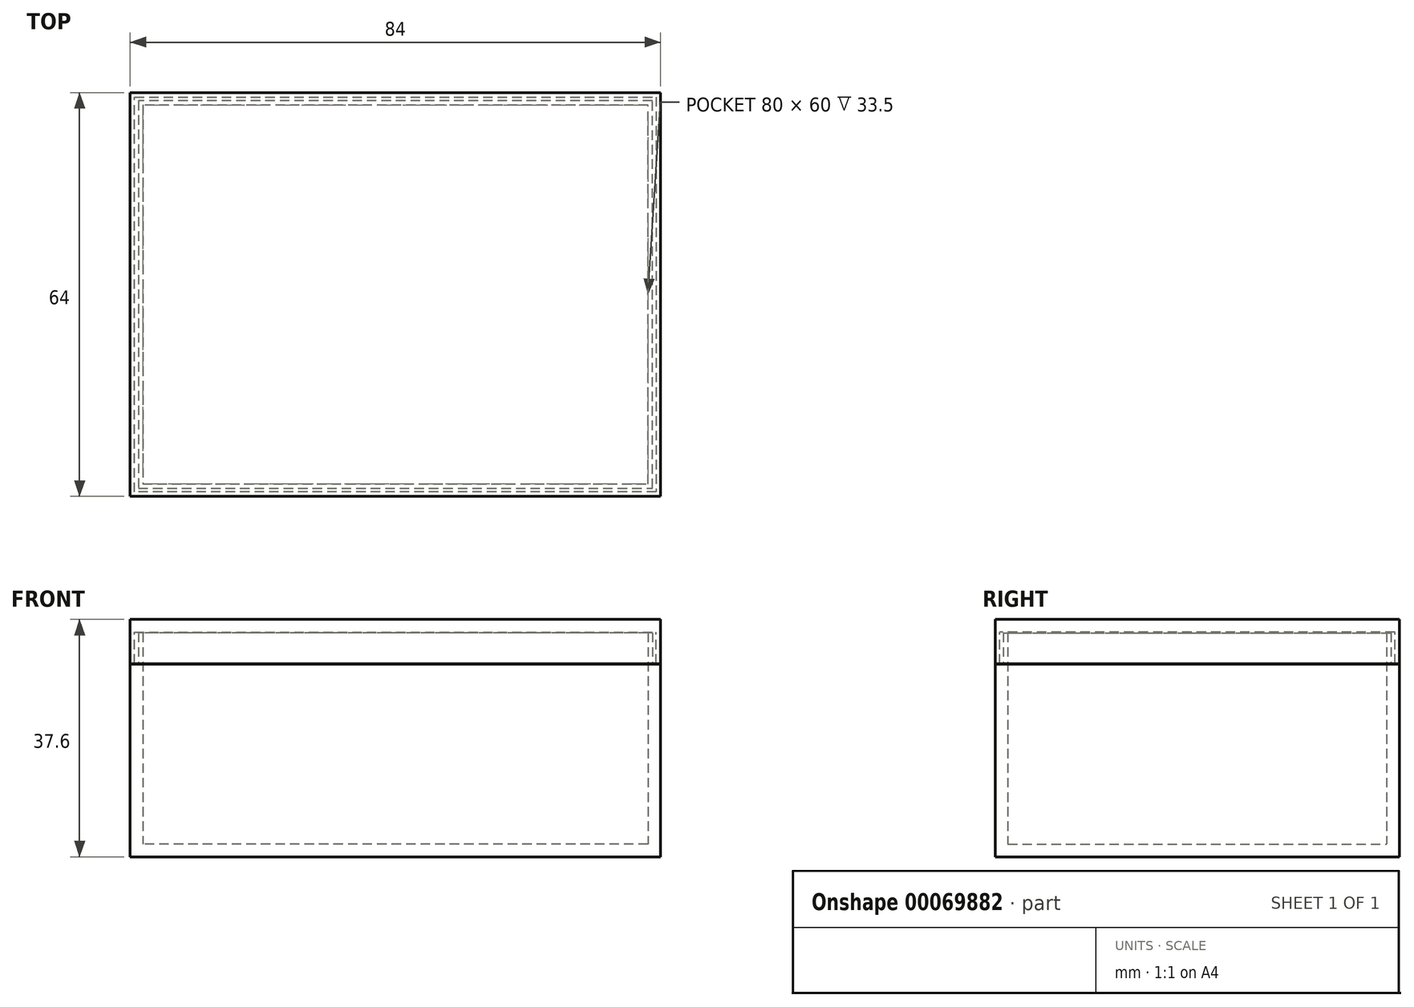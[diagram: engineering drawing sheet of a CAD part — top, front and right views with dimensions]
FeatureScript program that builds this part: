
annotation { "Feature Type Name" : "Feature", "Feature Type Description" : "" }
export const myFeature = defineFeature(function(context is Context, id is Id, definition is map)
    precondition{}
    {
        {
            var Q0;
            Q0=qCreatedBy(makeId("Top.planeOp"),FACE);
            var sketch = newSketch(context, id + "F0", { "sketchPlane" : qUnion([Q0])});
            skLineSegment(sketch, "E0.rect.bottom", {"start": v(42, -32) * mm, "end": v(-42, -32) * mm});
            skLineSegment(sketch, "E0.rect.top", {"start": v(42, 32) * mm, "end": v(-42, 32) * mm});
            skLineSegment(sketch, "E0.rect.left", {"start": v(42, -32) * mm, "end": v(42, 32) * mm});
            skLineSegment(sketch, "E0.rect.right", {"start": v(-42, -32) * mm, "end": v(-42, 32) * mm});
            skPoint(sketch, "E0.rect.middle", {"position": v(0, 0) * mm});
            skSolve(sketch);
        }
        {
            var Q0;
            Q0=qSketchRegion(id+"F0",true);
            extrude(context, id + "F1", {"entities" : qUnion([Q0]), "depth" : 2 * mm});
        }
        {
            var Q0;
            Q0=makeQuery(id+"F1.opExtrude","CAP_FACE",FACE,{"disambiguationData":[OSD([sQuery(id+"F0.wireOp",EDGE,"E0.rect.bottom"),sQuery(id+"F0.wireOp",EDGE,"E0.rect.top"),sQuery(id+"F0.wireOp",EDGE,"E0.rect.left"),sQuery(id+"F0.wireOp",EDGE,"E0.rect.right")])],"isStart":false});
            var sketch = newSketch(context, id + "F2", { "sketchPlane" : qUnion([Q0])});
            skLineSegment(sketch, "E1.0.0", {"start": v(-42, -32) * mm, "end": v(42, -32) * mm});
            skLineSegment(sketch, "E1.0.1", {"start": v(42, -32) * mm, "end": v(42, 32) * mm});
            skLineSegment(sketch, "E1.0.2", {"start": v(42, 32) * mm, "end": v(-42, 32) * mm});
            skLineSegment(sketch, "E1.0.3", {"start": v(-42, 32) * mm, "end": v(-42, -32) * mm});
            skLineSegment(sketch, "E2.0", {"start": v(40, 30) * mm, "end": v(-40, 30) * mm});
            skLineSegment(sketch, "E2.1", {"start": v(40, -30) * mm, "end": v(40, 30) * mm});
            skLineSegment(sketch, "E2.2", {"start": v(-40, -30) * mm, "end": v(40, -30) * mm});
            skLineSegment(sketch, "E2.3", {"start": v(-40, 30) * mm, "end": v(-40, -30) * mm});
            skSolve(sketch);
        }
        {
            var Q0;
            Q0=qSketchRegion(id+"F2",true);
            extrude(context, id + "F3", {"entities" : qUnion([Q0]), "operationType" : NewBodyOperationType.ADD, "depth" : 28.5 * mm});
        }
        {
            var Q0;
            Q0=makeQuery(id+"F3.opExtrude","CAP_FACE",FACE,{"disambiguationData":[OSD([sQuery(id+"F2.wireOp",EDGE,"E1.0.0"),sQuery(id+"F2.wireOp",EDGE,"E1.0.1"),sQuery(id+"F2.wireOp",EDGE,"E1.0.2"),sQuery(id+"F2.wireOp",EDGE,"E1.0.3"),sQuery(id+"F2.wireOp",EDGE,"E2.0"),sQuery(id+"F2.wireOp",EDGE,"E2.1"),sQuery(id+"F2.wireOp",EDGE,"E2.2"),sQuery(id+"F2.wireOp",EDGE,"E2.3")])],"isStart":false});
            var sketch = newSketch(context, id + "F4", { "sketchPlane" : qUnion([Q0])});
            skLineSegment(sketch, "E3.0", {"start": v(-40, 30) * mm, "end": v(-40, -30) * mm});
            skLineSegment(sketch, "E4.0", {"start": v(40, 30) * mm, "end": v(-40, 30) * mm});
            skLineSegment(sketch, "E5.0", {"start": v(-40, -30) * mm, "end": v(40, -30) * mm});
            skLineSegment(sketch, "E6.0", {"start": v(40, -30) * mm, "end": v(40, 30) * mm});
            skLineSegment(sketch, "E7.0", {"start": v(40.7, 30.7) * mm, "end": v(-40.7, 30.7) * mm});
            skLineSegment(sketch, "E7.1", {"start": v(40.7, -30.7) * mm, "end": v(40.7, 30.7) * mm});
            skLineSegment(sketch, "E7.2", {"start": v(-40.7, -30.7) * mm, "end": v(40.7, -30.7) * mm});
            skLineSegment(sketch, "E7.3", {"start": v(-40.7, 30.7) * mm, "end": v(-40.7, -30.7) * mm});
            skSolve(sketch);
        }
        {
            var Q0;
            Q0=qSketchRegion(id+"F4",true);
            extrude(context, id + "F5", {"entities" : qUnion([Q0]), "operationType" : NewBodyOperationType.ADD, "depth" : 5 * mm});
        }
        {
            var Q0;
            Q0=makeQuery(id+"F5.opExtrude","CAP_FACE",FACE,{"disambiguationData":[OSD([sQuery(id+"F4.wireOp",EDGE,"E3.0"),sQuery(id+"F4.wireOp",EDGE,"E4.0"),sQuery(id+"F4.wireOp",EDGE,"E5.0"),sQuery(id+"F4.wireOp",EDGE,"E6.0"),sQuery(id+"F4.wireOp",EDGE,"E7.0"),sQuery(id+"F4.wireOp",EDGE,"E7.1"),sQuery(id+"F4.wireOp",EDGE,"E7.2"),sQuery(id+"F4.wireOp",EDGE,"E7.3")])],"isStart":false});
            cPlane(context, id + "F6", {"entities" : qUnion([Q0]), "cplaneType" : CPlaneType.OFFSET, "offset" : .1 * mm, "width" : 150 * mm, "height" : 150 * mm});
        }
        {
            var Q0;
            Q0=qCreatedBy(id+"F6.planeOp",FACE);
            var sketch = newSketch(context, id + "F7", { "sketchPlane" : qUnion([Q0])});
            skLineSegment(sketch, "E8.0.0", {"start": v(42, -32) * mm, "end": v(-42, -32) * mm});
            skLineSegment(sketch, "E8.0.1", {"start": v(-42, -32) * mm, "end": v(-42, 32) * mm});
            skLineSegment(sketch, "E8.0.2", {"start": v(-42, 32) * mm, "end": v(42, 32) * mm});
            skLineSegment(sketch, "E8.0.3", {"start": v(42, 32) * mm, "end": v(42, -32) * mm});
            skSolve(sketch);
        }
        {
            var Q0;
            Q0=qSketchRegion(id+"F7",true);
            extrude(context, id + "F8", {"entities" : qUnion([Q0]), "depth" : 2 * mm});
        }
        {
            var Q0;
            Q0=makeQuery(id+"F8.opExtrude","CAP_FACE",FACE,{"disambiguationData":[OSD([sQuery(id+"F7.wireOp",EDGE,"E8.0.0"),sQuery(id+"F7.wireOp",EDGE,"E8.0.1"),sQuery(id+"F7.wireOp",EDGE,"E8.0.2"),sQuery(id+"F7.wireOp",EDGE,"E8.0.3")])],"isStart":true});
            var sketch = newSketch(context, id + "F9", { "sketchPlane" : qUnion([Q0])});
            skLineSegment(sketch, "E9.0", {"start": v(42, -32) * mm, "end": v(42, 32) * mm});
            skLineSegment(sketch, "E10.0", {"start": v(42, 32) * mm, "end": v(-42, 32) * mm});
            skLineSegment(sketch, "E11.0", {"start": v(-42, 32) * mm, "end": v(-42, -32) * mm});
            skLineSegment(sketch, "E12.0", {"start": v(-42, -32) * mm, "end": v(42, -32) * mm});
            skLineSegment(sketch, "E13.0", {"start": v(41.3, -31.3) * mm, "end": v(41.3, 31.3) * mm});
            skLineSegment(sketch, "E13.1", {"start": v(-41.3, -31.3) * mm, "end": v(41.3, -31.3) * mm});
            skLineSegment(sketch, "E13.2", {"start": v(-41.3, 31.3) * mm, "end": v(-41.3, -31.3) * mm});
            skLineSegment(sketch, "E13.3", {"start": v(41.3, 31.3) * mm, "end": v(-41.3, 31.3) * mm});
            skSolve(sketch);
        }
        {
            var Q0;
            Q0=qSketchRegion(id+"F9",true);
            extrude(context, id + "F10", {"entities" : qUnion([Q0]), "operationType" : NewBodyOperationType.ADD, "depth" : 5 * mm});
        }
    });
